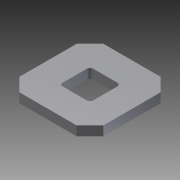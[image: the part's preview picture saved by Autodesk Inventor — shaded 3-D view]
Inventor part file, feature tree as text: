
AUTODESK INVENTOR PART (.ipt)
format: ipt  version: 2014 SP1 (Build 180222100, 222)  size: 449,536 bytes
history: native  units: in
note: dims shown in document units (in); Inventor stores cm internally (conversion verified against a paired STEP export)
features: other x1, imported_body x1, extrude x1, sketch x1
ambient origin geometry x8: Origin, YZ Plane, XZ Plane, XY Plane, X Axis, Y Axis, Z Axis, Center Point
bodies: Body1 (feature_tree)
feature tree (4):
  parser-record x1  (decoder bookkeeping rows leaked as tree rows — omitted from the tree; the rows remain in map.json)
  imported_body  "Base1"
  extrude  "Extrusion2"  Depth=0.5in TaperAngle=0.0deg
  sketch  "Sketch2"  dims[d2=0.5in d3=1.0in d4=0.0in]
